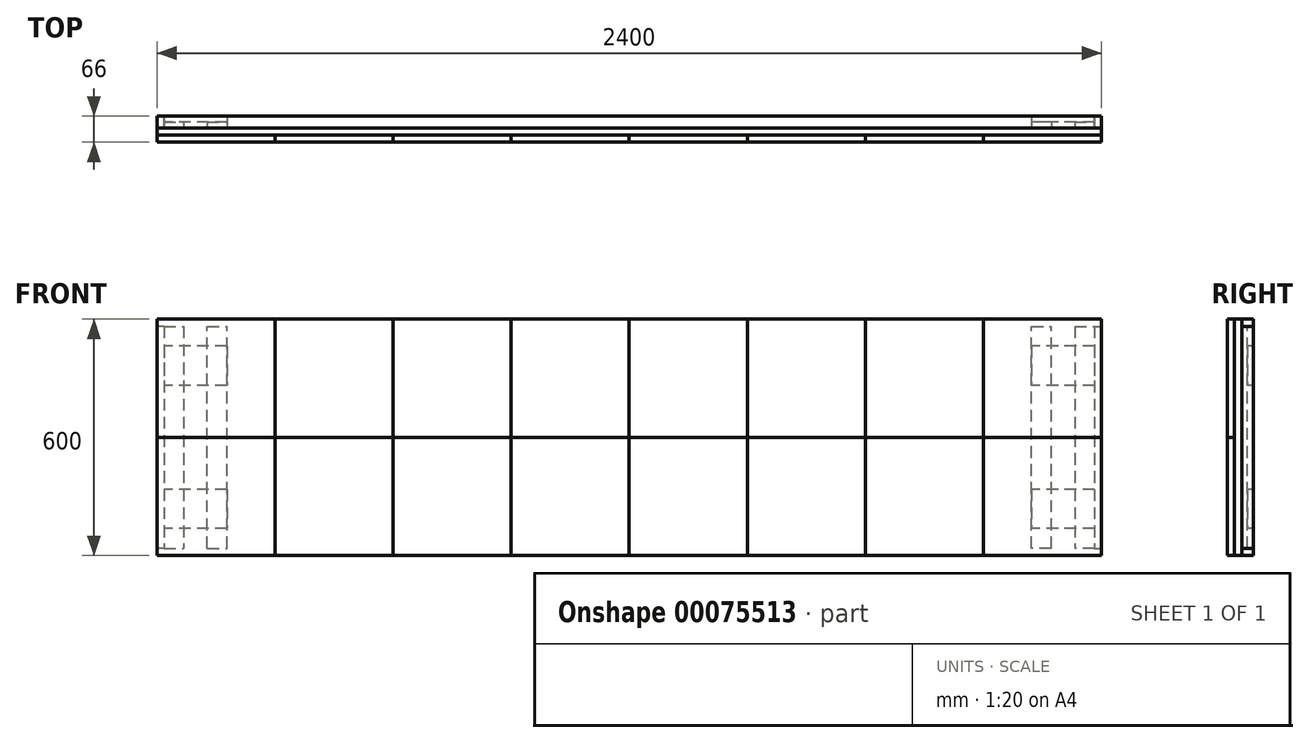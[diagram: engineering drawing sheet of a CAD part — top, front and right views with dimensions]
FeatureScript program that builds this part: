
annotation { "Feature Type Name" : "Feature", "Feature Type Description" : "" }
export const myFeature = defineFeature(function(context is Context, id is Id, definition is map)
    precondition{}
    {
        {
            var Q0;
            Q0=qCreatedBy(makeId("Front.planeOp"),FACE);
            var sketch = newSketch(context, id + "F0", { "sketchPlane" : qUnion([Q0])});
            skLineSegment(sketch, "E0.bottom", {"start": v(-869.84, 8.23) * mm, "end": v(1530.16, 8.23) * mm});
            skLineSegment(sketch, "E0.top", {"start": v(-869.84, -591.77) * mm, "end": v(-50, -591.77) * mm});
            skLineSegment(sketch, "E0.left", {"start": v(-869.84, 8.23) * mm, "end": v(-869.84, -591.77) * mm});
            skLineSegment(sketch, "E0.right", {"start": v(1530.16, 8.23) * mm, "end": v(1530.16, -591.77) * mm});
            skLineSegment(sketch, "E1.bottom", {"start": v(-851.84, -9.77) * mm, "end": v(1512.16, -9.77) * mm});
            skLineSegment(sketch, "E1.top", {"start": v(-851.84, -573.77) * mm, "end": v(-50, -573.77) * mm});
            skLineSegment(sketch, "E1.left", {"start": v(-851.84, -9.77) * mm, "end": v(-851.84, -573.77) * mm});
            skLineSegment(sketch, "E1.right", {"start": v(1512.16, -9.77) * mm, "end": v(1512.16, -573.77) * mm});
            skLineSegment(sketch, "E2", {"start": v(-851.84, -9.77) * mm, "end": v(-869.84, -9.77) * mm});
            skLineSegment(sketch, "E3", {"start": v(-851.84, -573.77) * mm, "end": v(-869.84, -573.77) * mm});
            skLineSegment(sketch, "E4", {"start": v(1512.16, -9.77) * mm, "end": v(1530.16, -9.77) * mm});
            skLineSegment(sketch, "E5", {"start": v(1512.16, -573.77) * mm, "end": v(1530.16, -573.77) * mm});
            skLineSegment(sketch, "E6.trimOffspring", {"start": v(50, -573.77) * mm, "end": v(1512.16, -573.77) * mm});
            skLineSegment(sketch, "E7.trimOffspring", {"start": v(50, -591.77) * mm, "end": v(1530.16, -591.77) * mm});
            skLineSegment(sketch, "E8", {"start": v(50, -573.77) * mm, "end": v(-50, -573.77) * mm});
            skLineSegment(sketch, "E9", {"start": v(-50, -591.77) * mm, "end": v(50, -591.77) * mm});
            skSolve(sketch);
        }
        {
            var Q0;
            Q0=makeQuery(id+"F0.imprint","IMPRINT",FACE,{"disambiguationData":[TD([[makeQuery(id+"F0.imprint","IMPRINT",EDGE,{"derivedFrom":sQuery(id+"F0.wireOp",EDGE,"E1.right")}),1.0]])]});
            extrude(context, id + "F1", {"entities" : qUnion([Q0]), "depth" : 30 * mm});
        }
        {
            var Q0;
            {var subQ1=sQuery(id+"F0.wireOp",EDGE,"E0.bottom");Q0=makeQuery(id+"F0.imprint","IMPRINT",FACE,{"disambiguationData":[TD([[makeQuery(id+"F0.imprint","IMPRINT",EDGE,{"derivedFrom":subQ1}),-1.0]])]});}
            extrude(context, id + "F2", {"entities" : qUnion([Q0]), "depth" : 30 * mm});
        }
        {
            var Q0;
            Q0=makeQuery(id+"F0.imprint","IMPRINT",FACE,{"disambiguationData":[TD([[makeQuery(id+"F0.imprint","IMPRINT",EDGE,{"derivedFrom":sQuery(id+"F0.wireOp",EDGE,"E1.left")}),-1.0]])]});
            extrude(context, id + "F3", {"entities" : qUnion([Q0]), "depth" : 30 * mm});
        }
        {
            var Q0;
            {var subQ1=sQuery(id+"F0.wireOp",EDGE,"E0.top");Q0=makeQuery(id+"F0.imprint","IMPRINT",FACE,{"disambiguationData":[TD([[makeQuery(id+"F0.imprint","IMPRINT",EDGE,{"derivedFrom":subQ1}),1.0]])]});}
            var Q1;
            {var subQ2=sQuery(id+"F0.wireOp",EDGE,"E5");Q1=makeQuery(id+"F0.imprint","IMPRINT",FACE,{"disambiguationData":[TD([[makeQuery(id+"F0.imprint","IMPRINT",EDGE,{"derivedFrom":subQ2}),-1.0]])]});}
            extrude(context, id + "F4", {"entities" : qUnion([Q0, Q1]), "depth" : 30 * mm});
        }
        {
            var Q0;
            Q0=makeQuery(id+"F2.opExtrude","CAP_FACE",FACE,{"disambiguationData":[OSD([sQuery(id+"F0.wireOp",EDGE,"E0.bottom"),sQuery(id+"F0.wireOp",EDGE,"E0.left"),sQuery(id+"F0.wireOp",EDGE,"E0.right"),sQuery(id+"F0.wireOp",EDGE,"E1.bottom"),sQuery(id+"F0.wireOp",EDGE,"E2"),sQuery(id+"F0.wireOp",EDGE,"E4")])],"isStart":false});
            var sketch = newSketch(context, id + "F5", { "sketchPlane" : qUnion([Q0])});
            skLineSegment(sketch, "E10.bottom", {"start": v(-869.84, 8.23) * mm, "end": v(1530.16, 8.23) * mm});
            skLineSegment(sketch, "E10.left", {"start": v(-869.84, 8.23) * mm, "end": v(-869.84, -591.77) * mm});
            skLineSegment(sketch, "E10.right", {"start": v(1530.16, 8.23) * mm, "end": v(1530.16, -591.77) * mm});
            skLineSegment(sketch, "E11", {"start": v(-869.84, -591.77) * mm, "end": v(1530.16, -591.77) * mm});
            skSolve(sketch);
        }
        {
            var Q0;
            Q0=qSketchRegion(id+"F5",true);
            extrude(context, id + "F6", {"entities" : qUnion([Q0]), "depth" : 18 * mm});
        }
        {
            var Q0;
            Q0=makeQuery(id+"F6.opExtrude","CAP_FACE",FACE,{"disambiguationData":[OSD([sQuery(id+"F5.wireOp",EDGE,"E10.bottom"),sQuery(id+"F5.wireOp",EDGE,"E10.top"),sQuery(id+"F5.wireOp",EDGE,"E10.left"),sQuery(id+"F5.wireOp",EDGE,"E10.right")])],"isStart":false});
            var sketch = newSketch(context, id + "F7", { "sketchPlane" : qUnion([Q0])});
            skLineSegment(sketch, "E12.bottom", {"start": v(-869.84, 8.23) * mm, "end": v(-569.84, 8.23) * mm});
            skLineSegment(sketch, "E12.top", {"start": v(-869.84, -291.77) * mm, "end": v(-569.84, -291.77) * mm});
            skLineSegment(sketch, "E12.left", {"start": v(-869.84, 8.23) * mm, "end": v(-869.84, -291.77) * mm});
            skLineSegment(sketch, "E12.right", {"start": v(-569.84, 8.23) * mm, "end": v(-569.84, -291.77) * mm});
            skLineSegment(sketch, "E13.1.0.0", {"start": v(-269.84, 8.23) * mm, "end": v(-269.84, -291.77) * mm});
            skLineSegment(sketch, "E13.1.0.1", {"start": v(-269.84, 8.23) * mm, "end": v(30.16, 8.23) * mm});
            skLineSegment(sketch, "E13.1.0.2", {"start": v(-269.84, -291.77) * mm, "end": v(30.16, -291.77) * mm});
            skLineSegment(sketch, "E13.1.0.3", {"start": v(30.16, 8.23) * mm, "end": v(30.16, -291.77) * mm});
            skLineSegment(sketch, "E13.2.0.0", {"start": v(330.16, 8.23) * mm, "end": v(330.16, -291.77) * mm});
            skLineSegment(sketch, "E13.2.0.1", {"start": v(330.16, 8.23) * mm, "end": v(630.16, 8.23) * mm});
            skLineSegment(sketch, "E13.2.0.2", {"start": v(330.16, -291.77) * mm, "end": v(630.16, -291.77) * mm});
            skLineSegment(sketch, "E13.2.0.3", {"start": v(630.16, 8.23) * mm, "end": v(630.16, -291.77) * mm});
            skLineSegment(sketch, "E13.3.0.0", {"start": v(930.16, 8.23) * mm, "end": v(930.16, -291.77) * mm});
            skLineSegment(sketch, "E13.3.0.1", {"start": v(930.16, 8.23) * mm, "end": v(1230.16, 8.23) * mm});
            skLineSegment(sketch, "E13.3.0.2", {"start": v(930.16, -291.77) * mm, "end": v(1230.16, -291.77) * mm});
            skLineSegment(sketch, "E13.3.0.3", {"start": v(1230.16, 8.23) * mm, "end": v(1230.16, -291.77) * mm});
            skLineSegment(sketch, "E13.direction1", {"start": v(-869.84, -291.77) * mm, "end": v(-269.84, -291.77) * mm, "construction": true});
            skLineSegment(sketch, "E14.bottom", {"start": v(-569.84, -291.77) * mm, "end": v(-269.84, -291.77) * mm});
            skLineSegment(sketch, "E14.top", {"start": v(-569.84, -591.77) * mm, "end": v(-269.84, -591.77) * mm});
            skLineSegment(sketch, "E14.left", {"start": v(-569.84, -291.77) * mm, "end": v(-569.84, -591.77) * mm});
            skLineSegment(sketch, "E14.right", {"start": v(-269.84, -291.77) * mm, "end": v(-269.84, -591.77) * mm});
            skLineSegment(sketch, "E15.1.0.0", {"start": v(330.16, -291.77) * mm, "end": v(330.16, -591.77) * mm});
            skLineSegment(sketch, "E15.1.0.1", {"start": v(30.16, -591.77) * mm, "end": v(330.16, -591.77) * mm});
            skLineSegment(sketch, "E15.1.0.2", {"start": v(30.16, -291.77) * mm, "end": v(330.16, -291.77) * mm});
            skLineSegment(sketch, "E15.1.0.3", {"start": v(30.16, -291.77) * mm, "end": v(30.16, -591.77) * mm});
            skLineSegment(sketch, "E15.2.0.0", {"start": v(930.16, -291.77) * mm, "end": v(930.16, -591.77) * mm});
            skLineSegment(sketch, "E15.2.0.1", {"start": v(630.16, -591.77) * mm, "end": v(930.16, -591.77) * mm});
            skLineSegment(sketch, "E15.2.0.2", {"start": v(630.16, -291.77) * mm, "end": v(930.16, -291.77) * mm});
            skLineSegment(sketch, "E15.2.0.3", {"start": v(630.16, -291.77) * mm, "end": v(630.16, -591.77) * mm});
            skLineSegment(sketch, "E15.direction1", {"start": v(-269.84, -591.77) * mm, "end": v(330.16, -591.77) * mm, "construction": true});
            skLineSegment(sketch, "E16.0.3.0", {"start": v(1530.16, -291.77) * mm, "end": v(1530.16, -591.77) * mm});
            skLineSegment(sketch, "E16.3.3.0", {"start": v(1230.16, -591.77) * mm, "end": v(1530.16, -591.77) * mm});
            skLineSegment(sketch, "E16.6.3.0", {"start": v(1230.16, -291.77) * mm, "end": v(1530.16, -291.77) * mm});
            skLineSegment(sketch, "E16.9.3.0", {"start": v(1230.16, -291.77) * mm, "end": v(1230.16, -591.77) * mm});
            skSolve(sketch);
        }
        {
            var Q0;
            Q0=qSketchRegion(id+"F7",true);
            extrude(context, id + "F8", {"entities" : qUnion([Q0]), "depth" : 18 * mm});
        }
        {
            var Q0;
            {var subQ2=sQuery(id+"F5.wireOp",EDGE,"E11");Q0=makeQuery(id+"F5.imprint","IMPRINT",FACE,{"disambiguationData":[TD([[makeQuery(id+"F5.imprint","IMPRINT",EDGE,{"derivedFrom":subQ2}),1.0]])]});}
            var sketch = newSketch(context, id + "F9", { "sketchPlane" : qUnion([Q0])});
            skLineSegment(sketch, "E17.bottom", {"start": v(1512.16, -9.77) * mm, "end": v(1462.16, -9.77) * mm});
            skLineSegment(sketch, "E17.top", {"start": v(1512.16, -573.77) * mm, "end": v(1462.16, -573.77) * mm});
            skLineSegment(sketch, "E17.left", {"start": v(1512.16, -9.77) * mm, "end": v(1512.16, -573.77) * mm});
            skLineSegment(sketch, "E17.right", {"start": v(1462.16, -9.77) * mm, "end": v(1462.16, -573.77) * mm});
            skLineSegment(sketch, "E18.bottom", {"start": v(-851.84, -9.77) * mm, "end": v(-801.84, -9.77) * mm});
            skLineSegment(sketch, "E18.top", {"start": v(-851.84, -573.77) * mm, "end": v(-801.84, -573.77) * mm});
            skLineSegment(sketch, "E18.left", {"start": v(-851.84, -9.77) * mm, "end": v(-851.84, -573.77) * mm});
            skLineSegment(sketch, "E18.right", {"start": v(-801.84, -9.77) * mm, "end": v(-801.84, -573.77) * mm});
            skLineSegment(sketch, "E19.bottom", {"start": v(1402.16, -573.77) * mm, "end": v(1352.16, -573.77) * mm});
            skLineSegment(sketch, "E19.top", {"start": v(1402.16, -9.77) * mm, "end": v(1352.16, -9.77) * mm});
            skLineSegment(sketch, "E19.left", {"start": v(1402.16, -573.77) * mm, "end": v(1402.16, -9.77) * mm});
            skLineSegment(sketch, "E19.right", {"start": v(1352.16, -573.77) * mm, "end": v(1352.16, -9.77) * mm});
            skLineSegment(sketch, "E20.bottom", {"start": v(-741.84, -573.77) * mm, "end": v(-691.84, -573.77) * mm});
            skLineSegment(sketch, "E20.top", {"start": v(-741.84, -9.77) * mm, "end": v(-691.84, -9.77) * mm});
            skLineSegment(sketch, "E20.left", {"start": v(-741.84, -573.77) * mm, "end": v(-741.84, -9.77) * mm});
            skLineSegment(sketch, "E20.right", {"start": v(-691.84, -573.77) * mm, "end": v(-691.84, -9.77) * mm});
            skSolve(sketch);
        }
        {
            var Q0;
            Q0=qSketchRegion(id+"F9",true);
            extrude(context, id + "F10", {"entities" : qUnion([Q0]), "oppositeDirection" : true, "depth" : 15 * mm});
        }
        {
            var Q0;
            Q0=makeQuery(id+"F10.opExtrude","CAP_FACE",FACE,{"disambiguationData":[OSD([sQuery(id+"F9.wireOp",EDGE,"E17.bottom"),sQuery(id+"F9.wireOp",EDGE,"E17.top"),sQuery(id+"F9.wireOp",EDGE,"E17.left"),sQuery(id+"F9.wireOp",EDGE,"E17.right")])],"isStart":false});
            var sketch = newSketch(context, id + "F11", { "sketchPlane" : qUnion([Q0])});
            skLineSegment(sketch, "E21.bottom", {"start": v(-1512.16, -59.77) * mm, "end": v(-1352.16, -59.77) * mm});
            skLineSegment(sketch, "E21.top", {"start": v(-1512.16, -159.77) * mm, "end": v(-1352.16, -159.77) * mm});
            skLineSegment(sketch, "E21.left", {"start": v(-1512.16, -59.77) * mm, "end": v(-1512.16, -159.77) * mm});
            skLineSegment(sketch, "E21.right", {"start": v(851.84, -59.77) * mm, "end": v(851.84, -159.77) * mm});
            skLineSegment(sketch, "E22.bottom", {"start": v(-1512.16, -423.77) * mm, "end": v(-1352.16, -423.77) * mm});
            skLineSegment(sketch, "E22.top", {"start": v(-1512.16, -523.77) * mm, "end": v(-1352.16, -523.77) * mm});
            skLineSegment(sketch, "E22.left", {"start": v(-1512.16, -423.77) * mm, "end": v(-1512.16, -523.77) * mm});
            skLineSegment(sketch, "E22.right", {"start": v(851.84, -423.77) * mm, "end": v(851.84, -523.77) * mm});
            skLineSegment(sketch, "E23", {"start": v(-1352.16, -59.77) * mm, "end": v(-1352.16, -159.77) * mm});
            skLineSegment(sketch, "E24", {"start": v(691.84, -59.77) * mm, "end": v(691.84, -159.77) * mm});
            skLineSegment(sketch, "E25.trimOffspring", {"start": v(691.84, -59.77) * mm, "end": v(851.84, -59.77) * mm});
            skLineSegment(sketch, "E26.trimOffspring", {"start": v(691.84, -159.77) * mm, "end": v(851.84, -159.77) * mm});
            skLineSegment(sketch, "E27.trimOffspring", {"start": v(691.84, -423.77) * mm, "end": v(851.84, -423.77) * mm});
            skLineSegment(sketch, "E28.trimOffspring", {"start": v(691.84, -523.77) * mm, "end": v(851.84, -523.77) * mm});
            skLineSegment(sketch, "E29.trimOffspring", {"start": v(691.84, -423.77) * mm, "end": v(691.84, -523.77) * mm});
            skLineSegment(sketch, "E30.trimOffspring", {"start": v(-1352.16, -423.77) * mm, "end": v(-1352.16, -523.77) * mm});
            skSolve(sketch);
        }
        {
            var Q0;
            Q0=qSketchRegion(id+"F11",true);
            extrude(context, id + "F12", {"entities" : qUnion([Q0]), "depth" : 15 * mm});
        }
    });
